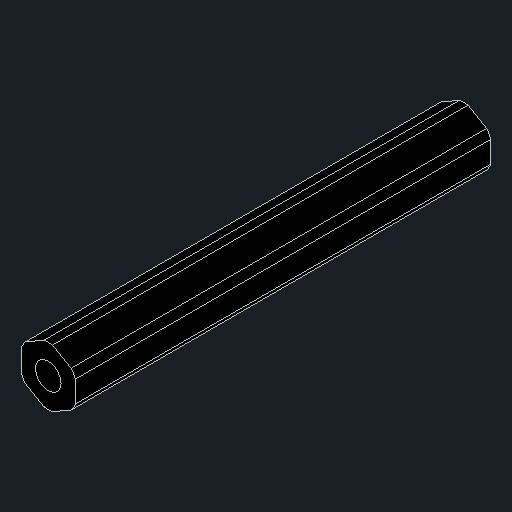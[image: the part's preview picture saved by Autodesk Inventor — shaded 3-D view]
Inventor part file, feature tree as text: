
AUTODESK INVENTOR PART (.ipt)
format: ipt  version: 2023.4 (Build 274418000, 418)  size: 256,000 bytes
history: native  units: in
note: dims shown in document units (in); Inventor stores cm internally (conversion verified against a paired STEP export)
features: extrude x2, projected_geometry x2, hole x1
ambient origin geometry x8: Origin, YZ Plane, XZ Plane, XY Plane, X Axis, Y Axis, Z Axis, Center Point
bodies: Solid1 (feature_tree)
feature tree (5):
  extrude  "Extrusion1"  TaperAngle=0.0deg  [1 undecoded]
  hole  "Hole1"  [1 undecoded]
  extrude  "Extrusion3"  TaperAngle=0.0deg  [1 undecoded]
  projected_geometry  "Project Cut Edges1"
  projected_geometry  "Project Cut Edges2"
note: 3 required parameter values undecoded (feature->parameter linkage not recoverable at this tier; creation-order binding heuristic only, values carry confidence <= 0.55)
